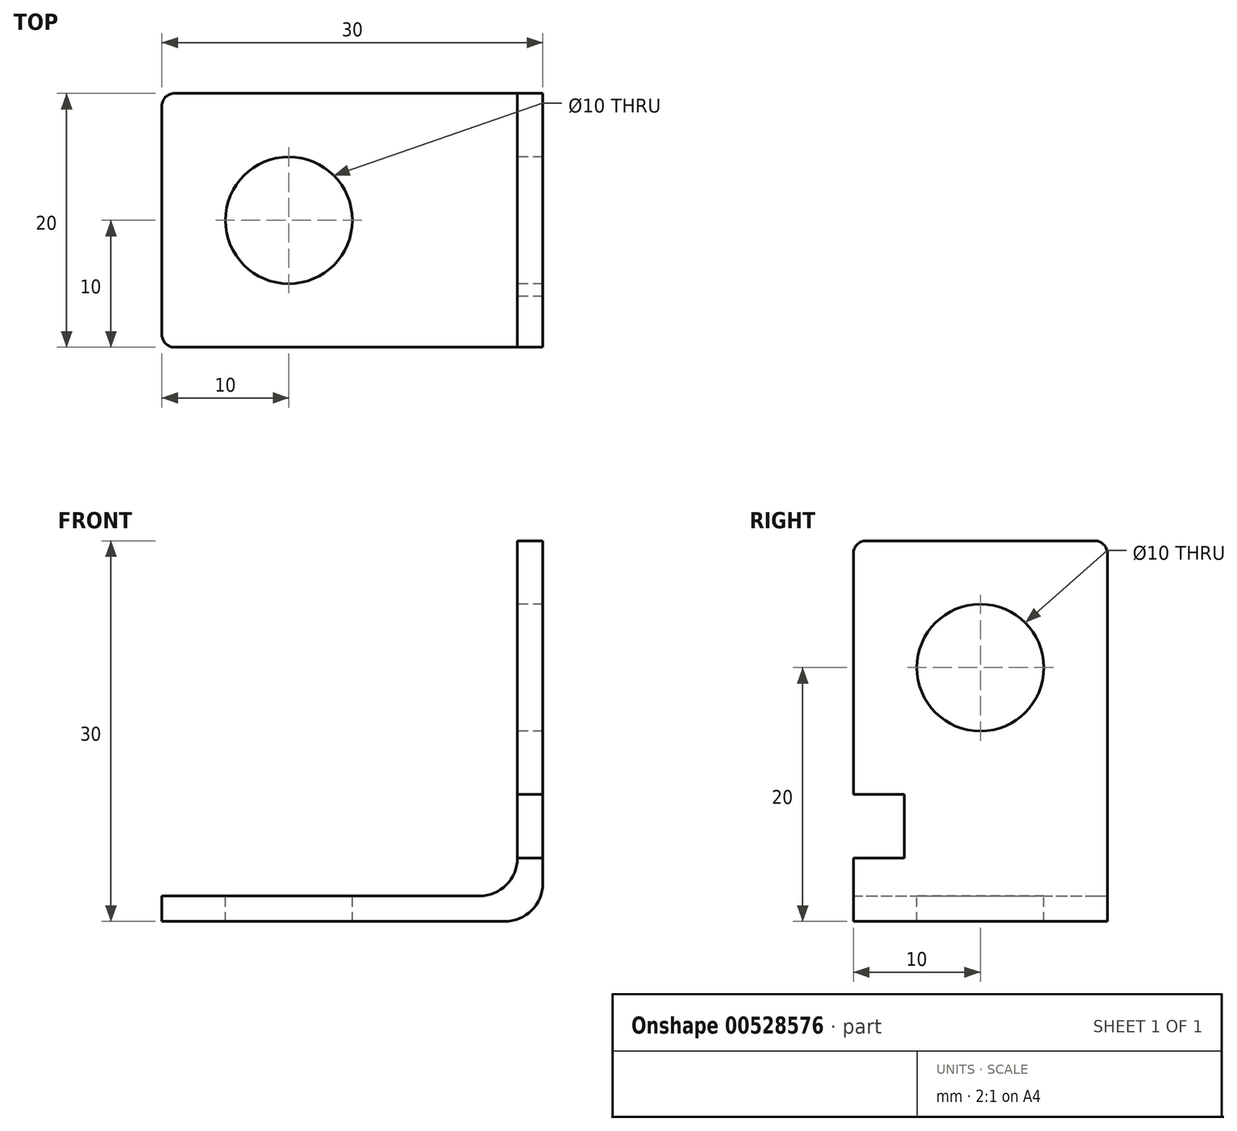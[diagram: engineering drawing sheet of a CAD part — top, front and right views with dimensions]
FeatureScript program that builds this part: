
annotation { "Feature Type Name" : "Feature", "Feature Type Description" : "" }
export const myFeature = defineFeature(function(context is Context, id is Id, definition is map)
    precondition{}
    {
        {
            var Q0;
            Q0=qCreatedBy(makeId("Front.planeOp"),FACE);
            var sketch = newSketch(context, id + "F0", { "sketchPlane" : qUnion([Q0])});
            skLineSegment(sketch, "E0", {"start": v(0, 0) * mm, "end": v(27, 0) * mm});
            skLineSegment(sketch, "E1", {"start": v(30, 3) * mm, "end": v(30, 30) * mm});
            skLineSegment(sketch, "E2", {"start": v(30, 30) * mm, "end": v(28, 30) * mm});
            skLineSegment(sketch, "E3", {"start": v(28, 30) * mm, "end": v(28, 5) * mm});
            skLineSegment(sketch, "E4", {"start": v(25, 2) * mm, "end": v(0, 2) * mm});
            skLineSegment(sketch, "E5", {"start": v(0, 2) * mm, "end": v(0, 0) * mm});
            skPoint(sketch, "E6.visualSharp", {"position": v(30, 0) * mm});
            skArc(sketch, "E6.filletArc", {"start": v(27, 0) * mm, "mid": v(29.12, 0.88) * mm, "end": v(30, 3) * mm});
            skPoint(sketch, "E7.visualSharp", {"position": v(28, 2) * mm});
            skArc(sketch, "E7.filletArc", {"start": v(25, 2) * mm, "mid": v(27.12, 2.88) * mm, "end": v(28, 5) * mm});
            skSolve(sketch);
        }
        {
            var Q0;
            Q0 = qSketchRegion(id + "F0", true);
            extrude(context, id + "F1", {"entities" : qUnion([Q0]), "depth" : 20 * mm, "offsetDistance" : 25 * mm});
        }
        {
            var Q0;
            Q0=makeQuery(id+"F1.opExtrude","SWEPT_FACE",FACE,{"disambiguationData":[OSD([sQuery(id+"F0.wireOp",EDGE,"E4")])]});
            var sketch = newSketch(context, id + "F2", { "sketchPlane" : qUnion([Q0])});
            skCircle(sketch, "E8", {"center": v(10, -10) * mm, "radius": 5 * mm});
            skSolve(sketch);
        }
        {
            var Q0;
            Q0 = qSketchRegion(id + "F2", true);
            extrude(context, id + "F3", {"entities" : qUnion([Q0]), "operationType" : NewBodyOperationType.REMOVE, "endBound" : BoundingType.THROUGH_ALL, "oppositeDirection" : true, "depth" : 25 * mm, "offsetDistance" : 25 * mm});
        }
        {
            var Q0;
            Q0=makeQuery(id+"F1.opExtrude","SWEPT_FACE",FACE,{"disambiguationData":[OSD([sQuery(id+"F0.wireOp",EDGE,"E3")])]});
            var sketch = newSketch(context, id + "F4", { "sketchPlane" : qUnion([Q0])});
            skCircle(sketch, "E9", {"center": v(10, 20) * mm, "radius": 5 * mm});
            skLineSegment(sketch, "E10.bottom", {"start": v(16, 5) * mm, "end": v(20, 5) * mm});
            skLineSegment(sketch, "E10.top", {"start": v(16, 10) * mm, "end": v(20, 10) * mm});
            skLineSegment(sketch, "E10.left", {"start": v(16, 5) * mm, "end": v(16, 10) * mm});
            skLineSegment(sketch, "E10.right", {"start": v(20, 5) * mm, "end": v(20, 10) * mm});
            skSolve(sketch);
        }
        {
            var Q0;
            Q0 = qSketchRegion(id + "F4", true);
            extrude(context, id + "F5", {"entities" : qUnion([Q0]), "operationType" : NewBodyOperationType.REMOVE, "endBound" : BoundingType.THROUGH_ALL, "oppositeDirection" : true, "depth" : 25 * mm, "offsetDistance" : 25 * mm});
        }
        {
            var Q0;
            Q0=makeQuery(id+"F1.opExtrude","CAP_EDGE",EDGE,{"disambiguationData":[OSD([sQuery(id+"F0.wireOp",EDGE,"E5")])],"isStart":false});
            var Q1;
            Q1=makeQuery(id+"F1.opExtrude","CAP_EDGE",EDGE,{"disambiguationData":[OSD([sQuery(id+"F0.wireOp",EDGE,"E2")])],"isStart":false});
            var Q2;
            Q2=makeQuery(id+"F1.opExtrude","CAP_EDGE",EDGE,{"disambiguationData":[OSD([sQuery(id+"F0.wireOp",EDGE,"E2")])],"isStart":true});
            var Q3;
            Q3=makeQuery(id+"F1.opExtrude","CAP_EDGE",EDGE,{"disambiguationData":[OSD([sQuery(id+"F0.wireOp",EDGE,"E5")])],"isStart":true});
            fillet(context, id + "F6", {"entities" : qUnion([Q0, Q1, Q2, Q3]), "radius" : 1 * mm, "tangentPropagation" : true, "allowEdgeOverflow" : false});
        }
    });
